# Revit family: Wall_Protection-Palladium Rigid Sheet-Vertical-Inpro
name_source: partatom
category: Specialty Equipment
units: mm (PartAtom-declared; Revit-internal decimal feet)

## family parameters
Always vertical = Yes
Cut with Voids When Loaded = No
Part Type = Normal
Room Calculation Point = No
Round Connector Dimension = Use Diameter
Shared = No
Work Plane-Based = No

## types (4) — shared parameters
Default Elevation = 0' - 0"
Description = Palladium® Rigid Vinyl Sheet
Inpro ISO# = BIMIPC.108
Manufacturer = Inpro®
Revision = Rev2
URL = https://www.inprocorp.com

## per-type parameters (varying)
| type | Palladium Sheet Thickness | Type Comments |
| 403 | 0' - 0 1/32" | 4'x8' or 4'x10' Sheet, .030" Thick |
| 410 | 0' - 0 3/32" | 4'x8' or 4'x10' Sheet, .080" Thick |
| 405 | 0' - 0 1/32" | 4'x8' or 4'x10' Sheet, .040" Thick |
| 406 | 0' - 0 1/16" | 4'x8' or 4'x10' Sheet, .060" Thick |

note: column(s) folded — value = type name in every type: Model

## geometry (parser evidence)
native form markers: Blend x2, Sweep x3
no freeform markers — native parametric forms only
